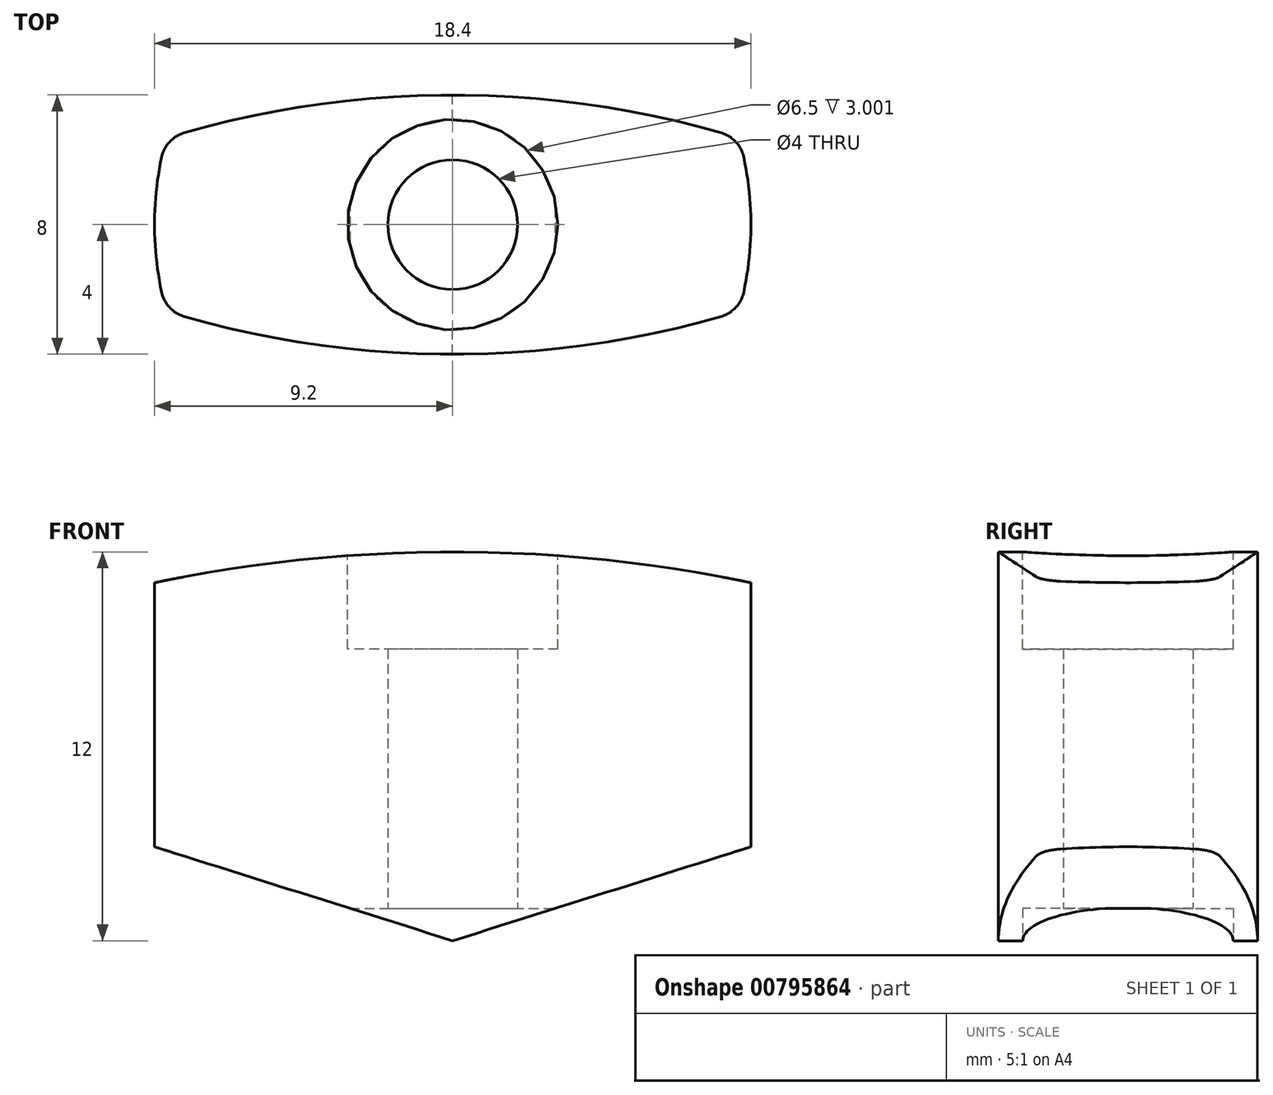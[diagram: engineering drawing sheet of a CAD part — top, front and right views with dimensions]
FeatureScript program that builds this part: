
annotation { "Feature Type Name" : "Feature", "Feature Type Description" : "" }
export const myFeature = defineFeature(function(context is Context, id is Id, definition is map)
    precondition{}
    {
        {
            var Q0;
            Q0=qCreatedBy(makeId("Top.planeOp"),FACE);
            var sketch = newSketch(context, id + "F0", { "sketchPlane" : qUnion([Q0])});
            skLineSegment(sketch, "E0.bottom", {"start": v(-9.2, 4) * mm, "end": v(9.2, 4) * mm, "construction": true});
            skLineSegment(sketch, "E0.top", {"start": v(-9.2, -4) * mm, "end": v(9.2, -4) * mm, "construction": true});
            skLineSegment(sketch, "E0.left", {"start": v(-9.2, 4) * mm, "end": v(-9.2, -4) * mm, "construction": true});
            skLineSegment(sketch, "E0.right", {"start": v(9.2, 4) * mm, "end": v(9.2, -4) * mm, "construction": true});
            skArc(sketch, "E1", {"start": v(-8.84, 2.67) * mm, "mid": v(0, 4) * mm, "end": v(8.84, 2.67) * mm});
            skArc(sketch, "E2", {"start": v(-8.84, -2.67) * mm, "mid": v(0, -4) * mm, "end": v(8.84, -2.67) * mm});
            skArc(sketch, "E3", {"start": v(-8.84, 2.67) * mm, "mid": v(-9.2, 0) * mm, "end": v(-8.84, -2.67) * mm});
            skArc(sketch, "E4", {"start": v(8.84, 2.67) * mm, "mid": v(9.2, 0) * mm, "end": v(8.84, -2.67) * mm});
            skSolve(sketch);
        }
        {
            var Q0;
            Q0 = qSketchRegion(id + "F0", true);
            extrude(context, id + "F1", {"entities" : qUnion([Q0]), "depth" : 12 * mm, "offsetDistance" : 25 * mm});
        }
        {
            var Q0;
            Q0=makeQuery(id+"F1.opExtrude","CAP_FACE",FACE,{"disambiguationData":[OSD([sQuery(id+"F0.wireOp",EDGE,"E1"),sQuery(id+"F0.wireOp",EDGE,"E2"),sQuery(id+"F0.wireOp",EDGE,"E3"),sQuery(id+"F0.wireOp",EDGE,"E4")])],"isStart":true});
            var sketch = newSketch(context, id + "F2", { "sketchPlane" : qUnion([Q0])});
            skCircle(sketch, "E5", {"center": v(0, 0) * mm, "radius": 2 * mm});
            skSolve(sketch);
        }
        {
            var Q0;
            Q0=qCreatedBy(makeId("Front.planeOp"),FACE);
            var sketch = newSketch(context, id + "F3", { "sketchPlane" : qUnion([Q0])});
            skLineSegment(sketch, "E6", {"start": v(-9.2, 2.9) * mm, "end": v(0, 0) * mm});
            skLineSegment(sketch, "E7", {"start": v(0, 0) * mm, "end": v(9.2, 2.9) * mm});
            skLineSegment(sketch, "E8", {"start": v(9.2, 2.9) * mm, "end": v(9.2, -1) * mm});
            skLineSegment(sketch, "E9", {"start": v(9.2, -1) * mm, "end": v(-9.2, -1) * mm});
            skLineSegment(sketch, "E10", {"start": v(-9.2, -1) * mm, "end": v(-9.2, 2.9) * mm});
            skSolve(sketch);
        }
        {
            var Q0;
            Q0=makeQuery(id+"F1.opExtrude","CAP_FACE",FACE,{"disambiguationData":[OSD([sQuery(id+"F0.wireOp",EDGE,"E1"),sQuery(id+"F0.wireOp",EDGE,"E2"),sQuery(id+"F0.wireOp",EDGE,"E3"),sQuery(id+"F0.wireOp",EDGE,"E4")])],"isStart":true});
            var sketch = newSketch(context, id + "F4", { "sketchPlane" : qUnion([Q0])});
            skCircle(sketch, "E11", {"center": v(0, 0) * mm, "radius": 3.25 * mm});
            skSolve(sketch);
        }
        {
            var Q0;
            Q0 = qSketchRegion(id + "F4", true);
            extrude(context, id + "F5", {"entities" : qUnion([Q0]), "operationType" : NewBodyOperationType.REMOVE, "oppositeDirection" : true, "depth" : 1 * mm, "offsetDistance" : 25 * mm});
        }
        {
            var Q0;
            Q0 = qSketchRegion(id + "F3", true);
            extrude(context, id + "F6", {"entities" : qUnion([Q0]), "operationType" : NewBodyOperationType.REMOVE, "endBound" : BoundingType.SYMMETRIC, "depth" : 25 * mm, "offsetDistance" : 25 * mm});
        }
        {
            var Q0;
            Q0 = qSketchRegion(id + "F2", true);
            extrude(context, id + "F7", {"entities" : qUnion([Q0]), "operationType" : NewBodyOperationType.REMOVE, "oppositeDirection" : true, "depth" : 25 * mm, "offsetDistance" : 25 * mm});
        }
        {
            var Q0;
            Q0=makeQuery(id+"F1.opExtrude","CAP_FACE",FACE,{"disambiguationData":[OSD([sQuery(id+"F0.wireOp",EDGE,"E1"),sQuery(id+"F0.wireOp",EDGE,"E2"),sQuery(id+"F0.wireOp",EDGE,"E3"),sQuery(id+"F0.wireOp",EDGE,"E4")])],"isStart":false});
            var sketch = newSketch(context, id + "F8", { "sketchPlane" : qUnion([Q0])});
            skCircle(sketch, "E12", {"center": v(0, 0) * mm, "radius": 3.25 * mm});
            skSolve(sketch);
        }
        {
            var Q0;
            Q0 = qSketchRegion(id + "F8", true);
            extrude(context, id + "F9", {"entities" : qUnion([Q0]), "operationType" : NewBodyOperationType.REMOVE, "oppositeDirection" : true, "depth" : 3 * mm, "offsetDistance" : 25 * mm});
        }
        {
            var Q0;
            Q0=qCreatedBy(makeId("Front.planeOp"),FACE);
            var sketch = newSketch(context, id + "F10", { "sketchPlane" : qUnion([Q0])});
            skArc(sketch, "E13", {"start": v(-9.2, 11.05) * mm, "mid": v(0, 12) * mm, "end": v(9.2, 11.05) * mm});
            skLineSegment(sketch, "E14", {"start": v(9.2, 11.05) * mm, "end": v(9.2, 0) * mm});
            skLineSegment(sketch, "E15", {"start": v(9.2, 0) * mm, "end": v(-9.2, 0) * mm});
            skLineSegment(sketch, "E16", {"start": v(-9.2, 0) * mm, "end": v(-9.2, 11.05) * mm});
            skSolve(sketch);
        }
        {
            var Q0;
            Q0 = qSketchRegion(id + "F10", true);
            extrude(context, id + "F11", {"entities" : qUnion([Q0]), "operationType" : NewBodyOperationType.INTERSECT, "endBound" : BoundingType.SYMMETRIC, "depth" : 25 * mm, "offsetDistance" : 25 * mm});
        }
        {
            var Q0;
            Q0=makeQuery(id+"F11.boolean.opBoolean","INTERSECT",EDGE,{"derivedFrom":[makeQuery(id+"F1.opExtrude","SWEPT_FACE",FACE,{"disambiguationData":[OSD([sQuery(id+"F0.wireOp",EDGE,"E2")])]}),makeQuery(id+"F11.boolean.toolComplement.opBoolean","COPY",FACE,{"derivedFrom":makeQuery(id+"F11.opExtrude","SWEPT_FACE",FACE,{"disambiguationData":[OSD([sQuery(id+"F10.wireOp",EDGE,"E13")])]})})]});
            var Q1;
            Q1=makeQuery(id+"F11.boolean.opBoolean","INTERSECT",EDGE,{"derivedFrom":[makeQuery(id+"F1.opExtrude","SWEPT_FACE",FACE,{"disambiguationData":[OSD([sQuery(id+"F0.wireOp",EDGE,"E1")])]}),makeQuery(id+"F11.boolean.toolComplement.opBoolean","COPY",FACE,{"derivedFrom":makeQuery(id+"F11.opExtrude","SWEPT_FACE",FACE,{"disambiguationData":[OSD([sQuery(id+"F10.wireOp",EDGE,"E13")])]})})]});
            var Q2;
            Q2=makeQuery(id+"F11.boolean.opBoolean","INTERSECT",EDGE,{"derivedFrom":[makeQuery(id+"F1.opExtrude","SWEPT_FACE",FACE,{"disambiguationData":[OSD([sQuery(id+"F0.wireOp",EDGE,"E3")])]}),makeQuery(id+"F11.boolean.toolComplement.opBoolean","COPY",FACE,{"derivedFrom":makeQuery(id+"F11.opExtrude","SWEPT_FACE",FACE,{"disambiguationData":[OSD([sQuery(id+"F10.wireOp",EDGE,"E13")])]})})]});
            var Q3;
            Q3=makeQuery(id+"F11.boolean.opBoolean","INTERSECT",EDGE,{"derivedFrom":[makeQuery(id+"F1.opExtrude","SWEPT_FACE",FACE,{"disambiguationData":[OSD([sQuery(id+"F0.wireOp",EDGE,"E4")])]}),makeQuery(id+"F11.boolean.toolComplement.opBoolean","COPY",FACE,{"derivedFrom":makeQuery(id+"F11.opExtrude","SWEPT_FACE",FACE,{"disambiguationData":[OSD([sQuery(id+"F10.wireOp",EDGE,"E13")])]})})]});
            var Q4;
            Q4=makeQuery(id+"F1.opExtrude","SWEPT_EDGE",EDGE,{"disambiguationData":[OSD([sQuery(id+"F0.wireOp",EDGE,"E2"),sQuery(id+"F0.wireOp",EDGE,"E4")])]});
            var Q5;
            Q5=makeQuery(id+"F1.opExtrude","SWEPT_EDGE",EDGE,{"disambiguationData":[OSD([sQuery(id+"F0.wireOp",EDGE,"E2"),sQuery(id+"F0.wireOp",EDGE,"E3")])]});
            var Q6;
            Q6=makeQuery(id+"F1.opExtrude","SWEPT_EDGE",EDGE,{"disambiguationData":[OSD([sQuery(id+"F0.wireOp",EDGE,"E1"),sQuery(id+"F0.wireOp",EDGE,"E3")])]});
            var Q7;
            Q7=makeQuery(id+"F1.opExtrude","SWEPT_EDGE",EDGE,{"disambiguationData":[OSD([sQuery(id+"F0.wireOp",EDGE,"E1"),sQuery(id+"F0.wireOp",EDGE,"E4")])]});
            fillet(context, id + "F12", {"entities" : qUnion([Q0, Q1, Q2, Q3, Q4, Q5, Q6, Q7]), "radius" : 1 * mm, "tangentPropagation" : true, "allowEdgeOverflow" : false});
        }
    });
